MODEL slx_bcfbe5aa9c5e
KIND model
BLOCK [Clock] Clock
BLOCK [Scope] Controller Schedule
  DataFormat = StructureWithTime
  Floating = off
  LimitDataPoints = off
  NumInputPorts = 1
  Ports = [1]
  SaveName = nschedule
  ShowLegends = off
  TimeRange = 2
  YMax = 4
  YMin = 0.5
BLOCK [TransferFcn] DC Servo
  Denominator = [1 1 0]
  Numerator = [1000]
BLOCK [Display] Display
  Decimation = 1
  Lockdown = off
  Ports = [1]
BLOCK [From] From
  CloseFcn = tagdialog Close
  GotoTag = r
  TagVisibility = global
BLOCK [From] From1
  CloseFcn = tagdialog Close
  GotoTag = y
  TagVisibility = global
BLOCK [From] From2
  CloseFcn = tagdialog Close
  GotoTag = u
  TagVisibility = global
BLOCK [Goto] Goto
  GotoTag = r
  TagVisibility = global
BLOCK [Goto] Goto1
  GotoTag = y
  TagVisibility = global
BLOCK [Goto] Goto2
  GotoTag = u
  TagVisibility = global
BLOCK [Mux] Mux1
  DisplayOption = bar
  Inputs = 2
  Ports = [2, 1]
BLOCK [Scope] Network Schedule
  DataFormat = StructureWithTime
  Floating = off
  LimitDataPoints = off
  NumInputPorts = 1
  Ports = [1]
  SaveName = nschedule1
  ShowLegends = off
  TimeRange = 2
  YMax = 3.5
  YMin = 1
BLOCK [SignalGenerator] Reference
  Ports = [0, 1]
  WaveForm = square
BLOCK [Scope] Sensor//Actuator Schedule
  DataFormat = StructureWithTime
  Floating = off
  LimitDataPoints = off
  NumInputPorts = 1
  Ports = [1]
  SaveName = nschedule2
  ShowLegends = off
  TimeRange = 2
  YMax = 4
  YMin = 0.5
BLOCK [Reference] TrueTime Kernel (Controller Node)  REF=truetime/TrueTime Kernel  (lib defined in slx_0362a698a4ec)
  Ports = [1, 1]
  SourceBlock = truetime/TrueTime Kernel
  args = 0.0
  battery = off
  clockoffsetdrift = [0 0]
  label = 1: 3
  ninputsoutputs = [1 0]
  ntriggers = 0
  nwnodenbr = 3
  poweroutput = off
  schedoutput = on
  sfun = controller_init
  trigtype = rising
BLOCK [Reference] TrueTime Kernel (Interfering Node)  REF=truetime/TrueTime Kernel  (lib defined in slx_0362a698a4ec)
  Ports = [1]
  SourceBlock = truetime/TrueTime Kernel
  args = 0.3
  battery = off
  clockoffsetdrift = [0 0]
  label = 1: 1
  ninputsoutputs = [1 0]
  ntriggers = 0
  nwnodenbr = 1
  poweroutput = off
  schedoutput = off
  sfun = interference_init
  trigtype = rising
BLOCK [Reference] TrueTime Kernel (Sensor//Actuator Node)  REF=truetime/TrueTime Kernel  (lib defined in slx_0362a698a4ec)
  Ports = [1, 2]
  SourceBlock = truetime/TrueTime Kernel
  args = []
  battery = off
  clockoffsetdrift = [0 0]
  label = 1: 2
  ninputsoutputs = [1 1]
  ntriggers = 0
  nwnodenbr = 2
  poweroutput = off
  schedoutput = on
  sfun = sensor_actuator_init
  trigtype = rising
BLOCK [Reference] TrueTime Network  REF=truetime/TrueTime Network  (lib defined in slx_0362a698a4ec)
  NIT = 0
  Ports = [0, 1]
  QSortMode = FIFO
  SourceBlock = truetime/TrueTime Network
  SourceType = Real-Time Network
  bandwidths = [0.5 0.25 0.25]
  buftype = Common buffer
  dynSchedule = []
  irtSchedule = 0
  lossprob = 0
  memsize = 80000
  miniSlotSize = 40
  minsize = 80
  nnodes = 3
  nodeGraph = 0
  nrtLength = 0
  nwnbr = 1
  nwtype = CSMA/CD (Ethernet)
  overflow = Retransmit
  rate = 80000
  schedule = [1 2 1 3]
  scheduleoutput = on
  seed = 0
  slotsize = 80
  sync = 0
BLOCK [UniformRandomNumber] Uniform Random Number
  Minimum = 0
  SampleTime = 0.001
BLOCK [Scope] r, y; u
  DataFormat = StructureWithTime
  Floating = off
  LimitDataPoints = off
  NumInputPorts = 2
  Ports = [2]
  SaveName = y
  ShowLegends = off
  TimeRange = 2
  YMax = 2~2
  YMin = -2~-2
ANNOTATION (root): TrueTime 2.0 Networked Control System <copyright redacted>
LINE Clock:1 -> Display:1
NET DC Servo:1 -> Goto1:1, TrueTime Kernel (Sensor//Actuator Node):1
LINE From1:1 -> Mux1:1
LINE From2:1 -> r, y; u:2
LINE From:1 -> Mux1:2
LINE Mux1:1 -> r, y; u:1
NET Reference:1 -> Goto:1, TrueTime Kernel (Controller Node):1
LINE TrueTime Kernel (Controller Node):1 -> Controller Schedule:1
NET TrueTime Kernel (Sensor//Actuator Node):1 -> DC Servo:1, Goto2:1
LINE TrueTime Kernel (Sensor//Actuator Node):2 -> Sensor//Actuator Schedule:1
LINE TrueTime Network:1 -> Network Schedule:1
LINE Uniform Random Number:1 -> TrueTime Kernel (Interfering Node):1
note: NET lines group one-source signal fan-out (src -> all destinations, sorted); 1:1 wires keep LINE
